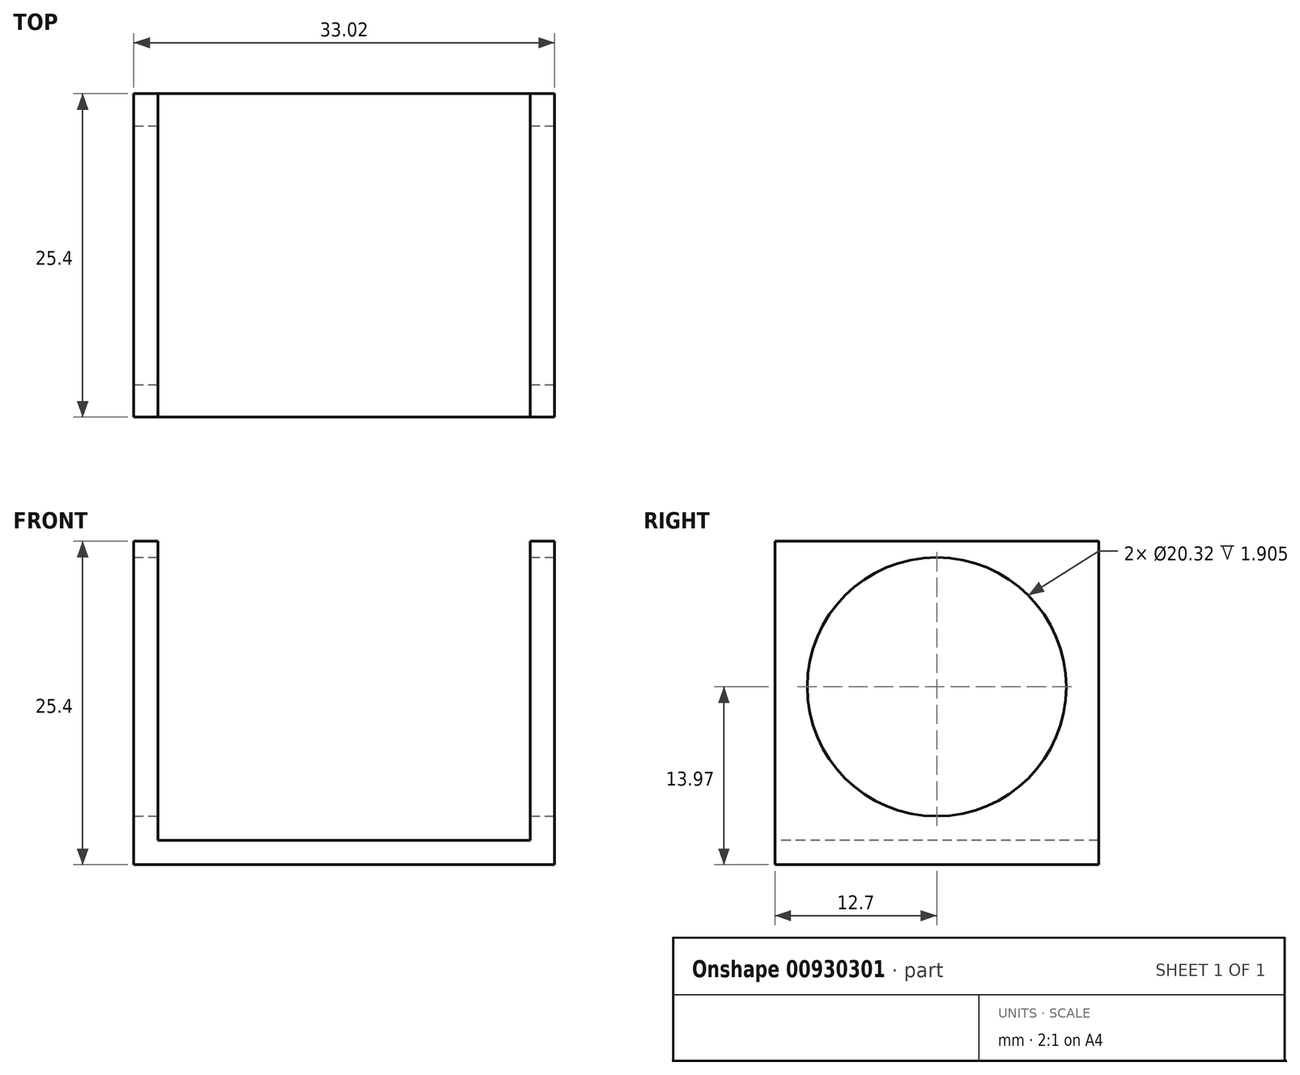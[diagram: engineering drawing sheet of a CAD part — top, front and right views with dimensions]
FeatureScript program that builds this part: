
annotation { "Feature Type Name" : "Feature", "Feature Type Description" : "" }
export const myFeature = defineFeature(function(context is Context, id is Id, definition is map)
    precondition{}
    {
        {
            var Q0;
            Q0=qCreatedBy(makeId("Top.planeOp"),FACE);
            var sketch = newSketch(context, id + "F0", { "sketchPlane" : qUnion([Q0])});
            skLineSegment(sketch, "E0.bottom", {"start": v(0, 0) * mm, "end": v(33.02, 0) * mm});
            skLineSegment(sketch, "E0.top", {"start": v(0, 25.4) * mm, "end": v(33.02, 25.4) * mm});
            skLineSegment(sketch, "E0.left", {"start": v(0, 0) * mm, "end": v(0, 25.4) * mm});
            skLineSegment(sketch, "E0.right", {"start": v(33.02, 0) * mm, "end": v(33.02, 25.4) * mm});
            skSolve(sketch);
        }
        {
            var Q0;
            Q0=makeQuery(id+"F0.imprint","IMPRINT",FACE,{"disambiguationData":[TD([[makeQuery(id+"F0.imprint","IMPRINT",EDGE,{"derivedFrom":sQuery(id+"F0.wireOp",EDGE,"E0.bottom")}),1.0]])]});
            extrude(context, id + "F1", {"entities" : qUnion([Q0]), "depth" : 25.4 * mm, "offsetDistance" : 25.4 * mm});
        }
        {
            var Q0;
            Q0=makeQuery(id+"F1.opExtrude","SWEPT_FACE",FACE,{"disambiguationData":[OSD([sQuery(id+"F0.wireOp",EDGE,"E0.right")])]});
            var sketch = newSketch(context, id + "F2", { "sketchPlane" : qUnion([Q0])});
            skCircle(sketch, "E1", {"center": v(12.7, 13.97) * mm, "radius": 10.16 * mm});
            skSolve(sketch);
        }
        {
            var Q0;
            Q0 = qSketchRegion(id + "F2", true);
            extrude(context, id + "F3", {"entities" : qUnion([Q0]), "operationType" : NewBodyOperationType.REMOVE, "oppositeDirection" : true, "depth" : 50.8 * mm, "offsetDistance" : 25.4 * mm});
        }
        {
            var Q0;
            Q0=makeQuery(id+"F1.opExtrude","SWEPT_FACE",FACE,{"disambiguationData":[OSD([sQuery(id+"F0.wireOp",EDGE,"E0.bottom")])]});
            var sketch = newSketch(context, id + "F4", { "sketchPlane" : qUnion([Q0])});
            skLineSegment(sketch, "E2.bottom", {"start": v(1.9, 25.4) * mm, "end": v(31.12, 25.4) * mm});
            skLineSegment(sketch, "E2.top", {"start": v(1.9, 1.9) * mm, "end": v(31.12, 1.9) * mm});
            skLineSegment(sketch, "E2.left", {"start": v(1.9, 25.4) * mm, "end": v(1.9, 1.9) * mm});
            skLineSegment(sketch, "E2.right", {"start": v(31.12, 25.4) * mm, "end": v(31.12, 1.9) * mm});
            skSolve(sketch);
        }
        {
            var Q0;
            Q0 = qSketchRegion(id + "F4", true);
            extrude(context, id + "F5", {"entities" : qUnion([Q0]), "operationType" : NewBodyOperationType.REMOVE, "oppositeDirection" : true, "depth" : 25.4 * mm, "offsetDistance" : 25.4 * mm});
        }
    });
